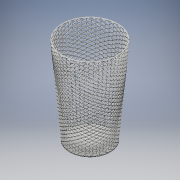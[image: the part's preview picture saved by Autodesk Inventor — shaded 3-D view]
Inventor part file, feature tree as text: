
AUTODESK INVENTOR PART (.ipt)
format: ipt  version: 2017 (Build 210142000, 142)  size: 31,996,928 bytes
history: native  units: in
note: dims shown in document units (in); Inventor stores cm internally (conversion verified against a paired STEP export)
features: sketch x3, other x2, revolve x1, extrude x1, fillet x1
ambient origin geometry x8: Origin, YZ Plane, XZ Plane, XY Plane, X Axis, Y Axis, Z Axis, Center Point
bodies: Solid1 (feature_tree)
feature tree (8):
  revolve  "Revolution1"  [1 undecoded]
  sketch  "Sketch3"  dims[d4=0.012in d5=90.0deg d6=0.3333in]
  other  "side wall"
  other  "side wall other"
  extrude  "bottom plate"  TaperAngle=90.0deg  [1 undecoded]
  fillet  "curve bottom"  Radius=0.3333in
  sketch  "Sketch2"  dims[d2=0.012in d3=0.3333in]
  sketch  "Sketch7"  dims[d7=0.012in d40=9.8425in d42=360.0deg d44=1.0in d45=1.0in d46=0.4134in d47=-0.0344in d48=90.0deg d49=90.0deg d50=0.0in d51=0.0in d52=1.0in d53=1.0in d54=0.4134in d55=-0.0344in d56=90.0deg d57=90.0deg d58=0.0in d59=0.0in d76=0.012in d77=0.0in d78=0.006in]
note: 2 required parameter values undecoded (feature->parameter linkage not recoverable at this tier; creation-order binding heuristic only, values carry confidence <= 0.55)